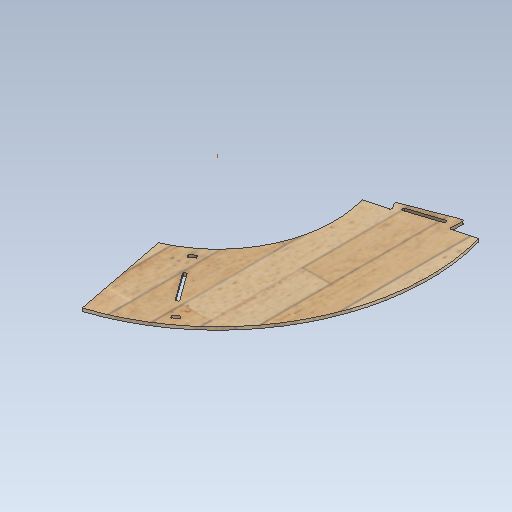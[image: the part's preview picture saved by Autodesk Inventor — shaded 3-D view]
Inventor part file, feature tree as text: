
AUTODESK INVENTOR PART (.ipt)
format: ipt  version: 2020 (Build 240168000, 168)  size: 457,728 bytes
history: native  units: mm
features: extrude x5, sketch x4, pattern_circular x3, mirror x2
ambient origin geometry x8: Origin, YZ Plane, XZ Plane, XY Plane, X Axis, Y Axis, Z Axis, Center Point
bodies: Body1 (feature_tree)
feature tree (14):
  extrude  "Extrusion3"  Depth=6.5mm
  extrude  "Extrusion4"  Depth=2.666667mm
  sketch  "Sketch3"  dims[d24=2.666667mm d25=2.666667mm]
  sketch  "Sketch5"  dims[d32=1.333333mm d33=1.333333mm]
  extrude  "Extrusion7"  Depth=1.333333mm
  pattern_circular  "Circular Pattern2"  [2 undecoded]
  pattern_circular  "Circular Pattern3"  [2 undecoded]
  mirror  "Mirror3"
  extrude  "Extrusion10"  Depth=0.5mm
  mirror  "Mirror4"
  pattern_circular  "Circular Pattern4"  [2 undecoded]
  extrude  "Extrusion11"  Depth=2.666667mm
  sketch  "Sketch2"  dims[d15=6.0mm d16=0.0mm d21=6.5mm]
  sketch  "Sketch6"  dims[d38=0.0mm d39=0.0mm d40=3.25mm d52=4.363323mm d60=0.872665mm d61=12.566371mm d62=13.439035mm d63=2.666667mm d64=0.523599mm d66=0.523599mm d67=2.666667mm d68=2.666667mm d70=12.566371mm d71=12.566371mm d84=467.42mm d85=850.0mm d86=658.71mm d87=150.07mm d88=425.0mm d89=4.363323mm d90=1.919862mm d91=1.919862mm d104=6.5mm d105=12.0mm d108=1.333333mm d109=1.333333mm d110=1.333333mm d111=1.333333mm d112=0.0mm d113=0.0mm d114=0.0mm d145=20.0mm d146=12.566371mm d149=145.0mm d150=90.0deg d151=90.0deg d152=90.0deg d153=90.0deg d154=20.0mm d155=25.132741mm d157=10.0mm d158=0.0mm d162=70.0mm d163=294.355mm d165=3.25mm d174=20.0mm d175=25.132741mm d177=0.0mm d178=0.0mm d176=0.5mm]
note: 6 required parameter values undecoded (feature->parameter linkage not recoverable at this tier; creation-order binding heuristic only, values carry confidence <= 0.55)
